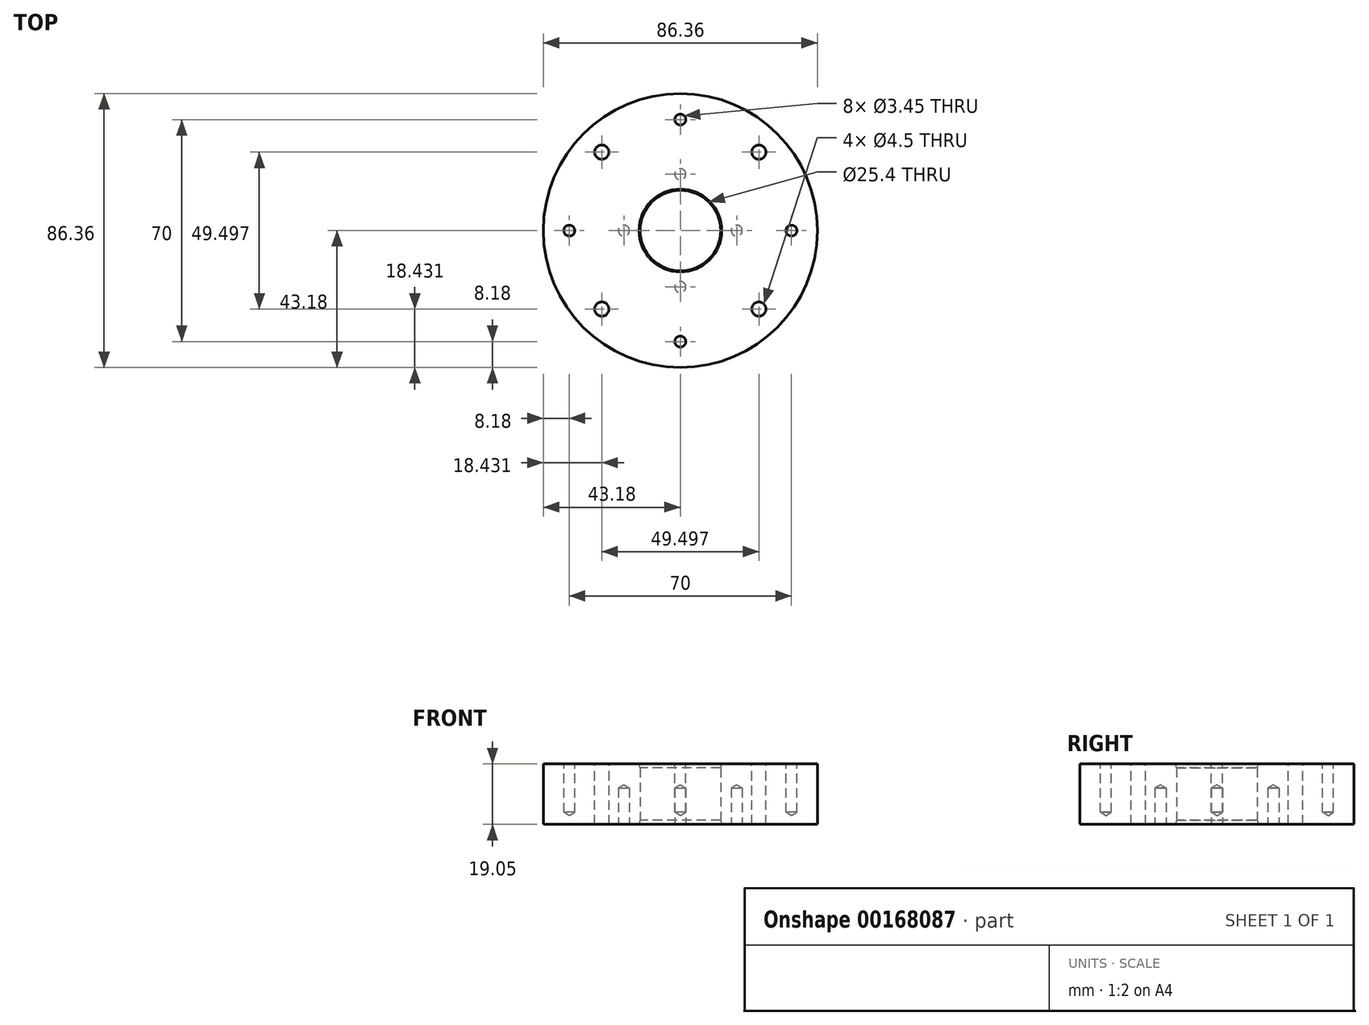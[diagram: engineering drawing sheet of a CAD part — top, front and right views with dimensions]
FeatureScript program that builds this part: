
annotation { "Feature Type Name" : "Feature", "Feature Type Description" : "" }
export const myFeature = defineFeature(function(context is Context, id is Id, definition is map)
    precondition{}
    {
        {
            var Q0;
            Q0=qCreatedBy(makeId("Top.planeOp"),FACE);
            var sketch = newSketch(context, id + "F0", { "sketchPlane" : qUnion([Q0])});
            skCircle(sketch, "E0", {"center": v(0, 0) * mm, "radius": 43.18 * mm});
            skCircle(sketch, "E1", {"center": v(0, 0) * mm, "radius": 12.7 * mm});
            skSolve(sketch);
        }
        {
            var Q0;
            Q0=qSketchRegion(id+"F0",true);
            extrude(context, id + "F1", {"entities" : qUnion([Q0]), "depth" : 19.05 * mm});
        }
        {
            var Q0;
            Q0=makeQuery(id+"F1.opExtrude","CAP_EDGE",EDGE,{"disambiguationData":[OSD([sQuery(id+"F0.wireOp",EDGE,"E1")])],"isStart":false});
            var Q1;
            Q1=makeQuery(id+"F1.opExtrude","CAP_EDGE",EDGE,{"disambiguationData":[OSD([sQuery(id+"F0.wireOp",EDGE,"E1")])],"isStart":true});
            chamfer(context, id + "F2", {"entities" : qUnion([Q0, Q1]), "chamferType" : ChamferType.OFFSET_ANGLE, "width" : 1.27 * mm, "oppositeDirection" : false, "angle" : 15 * degree, "tangentPropagation" : true});
        }
        {
            var Q0;
            Q0=makeQuery(id+"F1.opExtrude","CAP_FACE",FACE,{"disambiguationData":[OSD([sQuery(id+"F0.wireOp",EDGE,"E0"),sQuery(id+"F0.wireOp",EDGE,"E1")])],"isStart":true});
            var sketch = newSketch(context, id + "F3", { "sketchPlane" : qUnion([Q0])});
            skLineSegment(sketch, "E2", {"start": v(0, 0) * mm, "end": v(0, -12.7) * mm, "construction": true});
            skLineSegment(sketch, "E3", {"start": v(0, -12.7) * mm, "end": v(0, -22.86) * mm, "construction": true});
            skLineSegment(sketch, "E4", {"start": v(0, -22.86) * mm, "end": v(0, -12.7) * mm, "construction": true});
            skPoint(sketch, "E5", {"position": v(0, -17.78) * mm});
            skPoint(sketch, "E6.1.0", {"position": v(17.78, 0) * mm});
            skPoint(sketch, "E6.2.0", {"position": v(0, 17.78) * mm});
            skPoint(sketch, "E6.3.0", {"position": v(-17.78, 0) * mm});
            skPoint(sketch, "E6.center", {"position": v(0, 0) * mm});
            skSolve(sketch);
        }
        {
            var Q0;
            Q0=sQuery(id+"F3.wireOp",VERTEX,"E5");
            var Q1;
            Q1=sQuery(id+"F3.wireOp",VERTEX,"E6.3.0");
            var Q2;
            Q2=sQuery(id+"F3.wireOp",VERTEX,"E6.2.0");
            var Q3;
            Q3=sQuery(id+"F3.wireOp",VERTEX,"E6.1.0");
            var Q4;
            Q4=makeQuery(id+"F1.opExtrude","SWEPT_BODY",BODY,{"disambiguationData":[OSD([sQuery(id+"F0.wireOp",EDGE,"E0"),sQuery(id+"F0.wireOp",EDGE,"E1")])]});
            hole(context, id + "F4", {"style" : HoleStyle.SIMPLE, "endStyle" : HoleEndStyle.BLIND, "standardTappedOrClearance" : lookupTablePath({ "standard" : "ANSI", "engagement" : "75%", "pitch" : "32 tpi", "size" : "#8", "type" : "Tapped" }), "standardBlindInLast" : lookupTablePath({ "standard" : "ANSI", "engagement" : "75%", "pitch" : "32 tpi", "size" : "#8", "type" : "Tapped" }), "holeDiameter" : 3.45 * mm, "holeDepth" : 11.43 * mm, "locations" : qUnion([Q0, Q1, Q2, Q3]), "scope" : qUnion([Q4]), "majorDiameter" : 4.17 * mm});
        }
        {
            var Q0;
            Q0=makeQuery(id+"F1.opExtrude","CAP_FACE",FACE,{"disambiguationData":[OSD([sQuery(id+"F0.wireOp",EDGE,"E0"),sQuery(id+"F0.wireOp",EDGE,"E1")])],"isStart":false});
            var sketch = newSketch(context, id + "F5", { "sketchPlane" : qUnion([Q0])});
            skLineSegment(sketch, "E7", {"start": v(0, 0) * mm, "end": v(35, 0) * mm});
            skPoint(sketch, "E8", {"position": v(35, 0) * mm});
            skPoint(sketch, "E9.1.0", {"position": v(0, 35) * mm});
            skPoint(sketch, "E9.2.0", {"position": v(-35, 0) * mm});
            skPoint(sketch, "E9.3.0", {"position": v(0, -35) * mm});
            skPoint(sketch, "E9.center", {"position": v(0, 0) * mm});
            skSolve(sketch);
        }
        {
            var Q0;
            Q0=sQuery(id+"F5.wireOp",VERTEX,"E8");
            var Q1;
            Q1=sQuery(id+"F5.wireOp",VERTEX,"E9.3.0");
            var Q2;
            Q2=sQuery(id+"F5.wireOp",VERTEX,"E9.2.0");
            var Q3;
            Q3=sQuery(id+"F5.wireOp",VERTEX,"E9.1.0");
            var Q4;
            Q4=makeQuery(id+"F1.opExtrude","SWEPT_BODY",BODY,{"disambiguationData":[OSD([sQuery(id+"F0.wireOp",EDGE,"E0"),sQuery(id+"F0.wireOp",EDGE,"E1")])]});
            hole(context, id + "F6", {"style" : HoleStyle.SIMPLE, "endStyle" : HoleEndStyle.BLIND, "standardTappedOrClearance" : lookupTablePath({ "standard" : "ANSI", "engagement" : "75%", "pitch" : "32 tpi", "size" : "#8", "type" : "Tapped" }), "standardBlindInLast" : lookupTablePath({ "standard" : "ANSI", "engagement" : "75%", "pitch" : "32 tpi", "size" : "#8", "type" : "Tapped" }), "holeDiameter" : 3.45 * mm, "holeDepth" : 15.24 * mm, "locations" : qUnion([Q0, Q1, Q2, Q3]), "scope" : qUnion([Q4]), "majorDiameter" : 4.17 * mm});
        }
        {
            var Q0;
            Q0=makeQuery(id+"F1.opExtrude","CAP_FACE",FACE,{"disambiguationData":[OSD([sQuery(id+"F0.wireOp",EDGE,"E0"),sQuery(id+"F0.wireOp",EDGE,"E1")])],"isStart":false});
            var sketch = newSketch(context, id + "F7", { "sketchPlane" : qUnion([Q0])});
            skLineSegment(sketch, "E10", {"start": v(0, 0) * mm, "end": v(24.75, -24.75) * mm, "construction": true});
            skPoint(sketch, "E11", {"position": v(24.75, -24.75) * mm});
            skPoint(sketch, "E12.1.0", {"position": v(24.75, 24.75) * mm});
            skPoint(sketch, "E12.2.0", {"position": v(-24.75, 24.75) * mm});
            skPoint(sketch, "E12.3.0", {"position": v(-24.75, -24.75) * mm});
            skPoint(sketch, "E12.center", {"position": v(0, 0) * mm});
            skSolve(sketch);
        }
        {
            var Q0;
            Q0=sQuery(id+"F7.wireOp",VERTEX,"E11");
            var Q1;
            Q1=sQuery(id+"F7.wireOp",VERTEX,"E12.3.0");
            var Q2;
            Q2=sQuery(id+"F7.wireOp",VERTEX,"E12.2.0");
            var Q3;
            Q3=sQuery(id+"F7.wireOp",VERTEX,"E12.1.0");
            var Q4;
            Q4=makeQuery(id+"F1.opExtrude","SWEPT_BODY",BODY,{"disambiguationData":[OSD([sQuery(id+"F0.wireOp",EDGE,"E0"),sQuery(id+"F0.wireOp",EDGE,"E1")])]});
            hole(context, id + "F8", {"style" : HoleStyle.SIMPLE, "endStyle" : HoleEndStyle.THROUGH, "standardTappedOrClearance" : lookupTablePath({ "standard" : "ANSI", "fit" : "Normal (ASME)", "size" : "#8", "type" : "Clearance" }), "standardBlindInLast" : lookupTablePath({ "fit" : "Free", "standard" : "ANSI", "size" : "#8", "type" : "Clearance" }), "holeDiameter" : 4.5 * mm, "locations" : qUnion([Q0, Q1, Q2, Q3]), "scope" : qUnion([Q4]), "isTappedThrough" : true});
        }
    });
